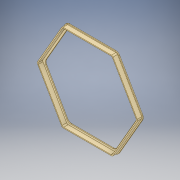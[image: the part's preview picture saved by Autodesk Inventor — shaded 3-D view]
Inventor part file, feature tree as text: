
AUTODESK INVENTOR PART (.ipt)
format: ipt  version: 2019 (Build 230136000, 136)  size: 374,784 bytes
history: native  units: mm
features: extrude x3, sketch x3, fillet x2, projected_geometry x2
ambient origin geometry x8: Origin, YZ Plane, XZ Plane, XY Plane, X Axis, Y Axis, Z Axis, Center Point
bodies: Solid1 (feature_tree)
feature tree (10):
  extrude  "Extrusion1"  Depth=2.0mm TaperAngle=0.0deg
  extrude  "Extrusion5"  Depth=2.0mm
  extrude  "Extrusion6"  Depth=4.0mm
  fillet  "Fillet1"  Radius=7.0mm
  fillet  "Fillet2"  Radius=10.0mm
  sketch  "Sketch1"  dims[d0=200.0mm d1=2.0mm d2=0.0mm]
  sketch  "Sketch5"  dims[d15=2.0mm d16=2.0mm]
  projected_geometry  "Projected Loop4"
  sketch  "Sketch7"  dims[d17=10.0mm d18=0.0mm d19=4.0mm d20=7.0mm d21=0.0mm d22=10.0mm d23=4.0mm d24=10.0mm]
  projected_geometry  "Projected Loop6"
